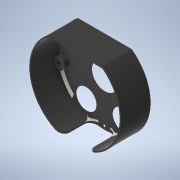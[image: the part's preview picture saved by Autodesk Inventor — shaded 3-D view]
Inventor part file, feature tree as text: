
AUTODESK INVENTOR PART (.ipt)
format: ipt  version: 2020.2 (Build 242310000, 310)  size: 581,120 bytes
history: native  units: mm
features: extrude x18, sketch x17, projected_geometry x13, fillet x2
ambient origin geometry x8: Origin, YZ Plane, XZ Plane, XY Plane, X Axis, Y Axis, Z Axis, Center Point
bodies: Solid1 (feature_tree)
feature tree (50):
  extrude  "Extrusion1"  Depth=55.0mm
  extrude  "Extrusion2"  Depth=40.0mm
  extrude  "Extrusion3"  Depth=35.0mm
  extrude  "Extrusion4"  Depth=54.772mm
  extrude  "Extrusion5"  Depth=50.0mm
  extrude  "Extrusion6"  Depth=1.0mm
  extrude  "Extrusion7"  Depth=43.0mm
  fillet  "Fillet1"  Radius=43.0mm
  extrude  "Extrusion8"  Depth=0.4mm TaperAngle=0.0deg
  extrude  "Extrusion9"  Depth=2.5mm TaperAngle=0.0deg
  extrude  "Extrusion10"  Depth=69.25mm
  extrude  "Extrusion11"  Depth=2.5mm TaperAngle=0.0deg
  fillet  "Fillet2"  Radius=150.0mm
  extrude  "Extrusion12"  Depth=10.0mm
  extrude  "Extrusion13"  Depth=56.0mm TaperAngle=0.0deg
  extrude  "Extrusion14"  Depth=1.0mm TaperAngle=0.0deg
  extrude  "Extrusion15"  Depth=5.0mm
  extrude  "Extrusion16"  Depth=82.0mm
  extrude  "Extrusion18"  Depth=82.0mm
  extrude  "Extrusion19"  TaperAngle=0.0deg  [1 undecoded]
  sketch  "Sketch1"  dims[d0=176.0mm d1=55.0mm]
  sketch  "Sketch2"  dims[d2=170.0mm d3=40.0mm]
  sketch  "Sketch3"  dims[d4=40.0mm d5=35.0mm]
  projected_geometry  "Projected Loop2"
  sketch  "Sketch6"  dims[d6=54.772mm d7=54.772mm]
  projected_geometry  "Projected Loop3"
  sketch  "Sketch7"  dims[d8=35.0mm d9=50.0mm]
  projected_geometry  "Projected Loop4"
  sketch  "Sketch8"  dims[d10=1.0mm d11=0.0mm d12=43.0mm]
  sketch  "Sketch9"  dims[d13=43.0mm d14=43.0mm d15=43.0mm]
  sketch  "Sketch10"  dims[d16=53.0mm d17=0.4mm d18=0.0mm]
  sketch  "Sketch11"  dims[d19=71.25mm d20=2.5mm d21=0.0mm]
  sketch  "Sketch12"  dims[d24=172.0mm d25=69.25mm]
  projected_geometry  "Projected Loop5"
  sketch  "Sketch13"  dims[d26=2.0mm d27=0.0mm d28=2.5mm d29=0.0mm d30=150.0mm]
  sketch  "Sketch14"  dims[d31=10.0mm d32=0.0mm d33=172.0mm]
  projected_geometry  "Projected Loop6"
  projected_geometry  "Projected Loop7"
  sketch  "Sketch15"  dims[d34=68.125mm d35=56.0mm d36=0.0mm]
  sketch  "Sketch16"  dims[d37=4.0mm d41=1.0mm d42=0.0mm]
  sketch  "Sketch17"  dims[d43=5.0mm d44=5.0mm]
  projected_geometry  "Projected Loop8"
  projected_geometry  "Projected Loop9"
  projected_geometry  "Projected Loop10"
  sketch  "Sketch19"  dims[d45=5.0mm d46=82.0mm]
  projected_geometry  "Projected Loop12"
  projected_geometry  "Projected Loop13"
  projected_geometry  "Projected Loop14"
  sketch  "Sketch20"  dims[d47=82.0mm d48=82.0mm d49=0.0mm d50=0.0mm d51=0.0mm d52=5.0mm d53=0.0mm d54=3.0mm d55=3.0mm d56=78.0mm d57=78.0mm d58=12.0mm d59=12.0mm d60=10.0mm d61=0.0mm d62=5.5mm d63=5.5mm d64=0.5mm d65=0.0mm d70=10.0mm d71=0.0mm d72=14.0mm d73=50.0mm d74=112.0mm d75=47.0mm d76=47.0mm d77=57.0mm d78=57.0mm d79=47.0mm d80=47.0mm d81=47.0mm d82=47.0mm d83=47.0mm d84=47.0mm d85=3.0mm d86=3.0mm d87=12.0mm d88=12.0mm d89=78.0mm d90=78.0mm d91=4.3mm d92=4.3mm d93=20.0mm d94=20.0mm d95=10.0mm d96=0.0mm d97=10.0mm d98=0.0mm d99=5.2mm d100=5.2mm d101=1.5mm d102=0.0mm d103=3.0mm d104=0.0mm d105=82.0mm d106=6.0mm d107=0.0mm d108=3.0mm d109=3.0mm d110=1.5mm d111=0.0mm d117=1.5mm d118=0.0mm d120=5.0mm d121=1.7mm d122=0.0mm d123=0.0mm d124=5.2mm d125=0.5mm d126=0.872665mm d127=0.5mm d128=0.872665mm]
  projected_geometry  "Projected Loop15"
note: 1 required parameter value undecoded (feature->parameter linkage not recoverable at this tier; creation-order binding heuristic only, values carry confidence <= 0.55)
